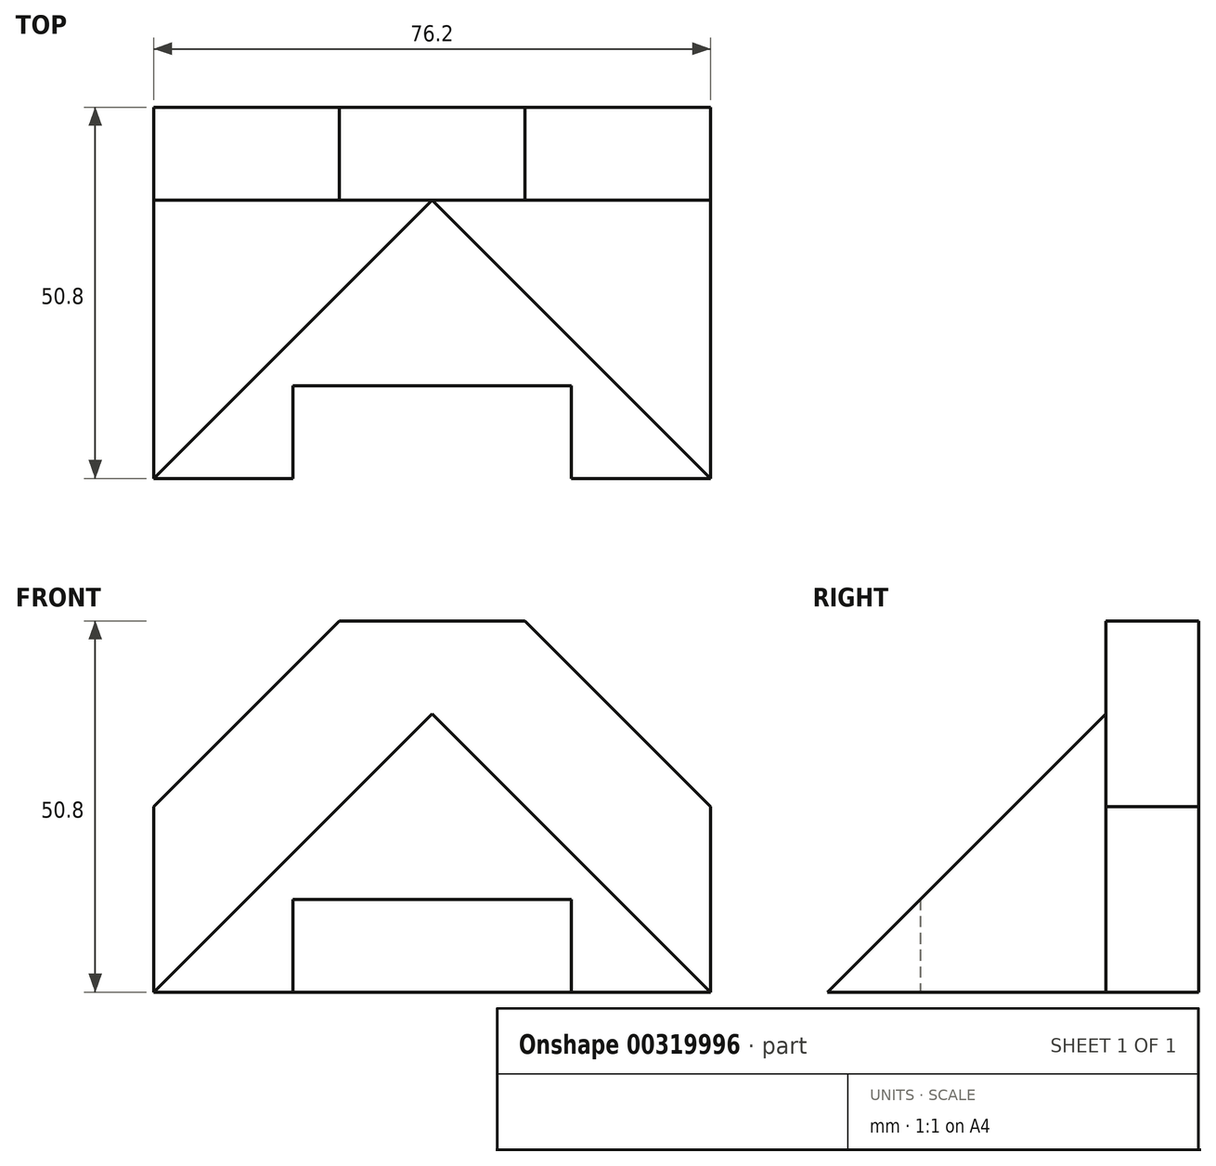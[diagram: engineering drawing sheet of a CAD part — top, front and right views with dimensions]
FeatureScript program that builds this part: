
annotation { "Feature Type Name" : "Feature", "Feature Type Description" : "" }
export const myFeature = defineFeature(function(context is Context, id is Id, definition is map)
    precondition{}
    {
        {
            var Q0;
            Q0=qCreatedBy(makeId("Front.planeOp"),FACE);
            var sketch = newSketch(context, id + "F0", { "sketchPlane" : qUnion([Q0])});
            skLineSegment(sketch, "E0.bottom", {"start": v(0, 0) * mm, "end": v(76.2, 0) * mm});
            skLineSegment(sketch, "E0.top", {"start": v(0, 50.8) * mm, "end": v(76.2, 50.8) * mm});
            skLineSegment(sketch, "E0.left", {"start": v(0, 0) * mm, "end": v(0, 50.8) * mm});
            skLineSegment(sketch, "E0.right", {"start": v(76.2, 0) * mm, "end": v(76.2, 50.8) * mm});
            skSolve(sketch);
        }
        {
            var Q0;
            Q0 = qSketchRegion(id + "F0", true);
            extrude(context, id + "F1", {"entities" : qUnion([Q0]), "depth" : 12.7 * mm});
        }
        {
            var Q0;
            Q0=makeQuery(id+"F1.opExtrude","CAP_FACE",FACE,{"disambiguationData":[OSD([sQuery(id+"F0.wireOp",EDGE,"E0.bottom"),sQuery(id+"F0.wireOp",EDGE,"E0.top"),sQuery(id+"F0.wireOp",EDGE,"E0.left"),sQuery(id+"F0.wireOp",EDGE,"E0.right")])],"isStart":false});
            var sketch = newSketch(context, id + "F2", { "sketchPlane" : qUnion([Q0])});
            skLineSegment(sketch, "E1", {"start": v(0, 25.4) * mm, "end": v(25.4, 50.8) * mm});
            skLineSegment(sketch, "E2", {"start": v(50.8, 50.8) * mm, "end": v(76.2, 25.4) * mm});
            skLineSegment(sketch, "E3", {"start": v(0, 25.4) * mm, "end": v(0, 50.8) * mm});
            skLineSegment(sketch, "E4", {"start": v(0, 50.8) * mm, "end": v(25.4, 50.8) * mm});
            skLineSegment(sketch, "E5", {"start": v(50.8, 50.8) * mm, "end": v(76.2, 50.8) * mm});
            skLineSegment(sketch, "E6", {"start": v(76.2, 50.8) * mm, "end": v(76.2, 25.4) * mm});
            skSolve(sketch);
        }
        {
            var Q0;
            Q0 = qSketchRegion(id + "F2", true);
            extrude(context, id + "F3", {"entities" : qUnion([Q0]), "operationType" : NewBodyOperationType.REMOVE, "oppositeDirection" : true, "depth" : 12.7 * mm});
        }
        {
            var Q0;
            Q0=makeQuery(id+"F1.opExtrude","CAP_FACE",FACE,{"disambiguationData":[OSD([sQuery(id+"F0.wireOp",EDGE,"E0.bottom"),sQuery(id+"F0.wireOp",EDGE,"E0.top"),sQuery(id+"F0.wireOp",EDGE,"E0.left"),sQuery(id+"F0.wireOp",EDGE,"E0.right")])],"isStart":false});
            var sketch = newSketch(context, id + "F4", { "sketchPlane" : qUnion([Q0])});
            skLineSegment(sketch, "E7", {"start": v(0, 0) * mm, "end": v(38.1, 38.1) * mm});
            skLineSegment(sketch, "E8", {"start": v(38.1, 38.1) * mm, "end": v(76.2, 0) * mm});
            skLineSegment(sketch, "E9", {"start": v(0, 0) * mm, "end": v(76.2, 0) * mm});
            skSolve(sketch);
        }
        {
            var Q0;
            Q0 = qSketchRegion(id + "F4", true);
            extrude(context, id + "F5", {"entities" : qUnion([Q0]), "operationType" : NewBodyOperationType.ADD, "depth" : 38.1 * mm});
        }
        {
            var Q0;
            Q0=qCreatedBy(makeId("Right.planeOp"),FACE);
            var sketch = newSketch(context, id + "F6", { "sketchPlane" : qUnion([Q0])});
            skLineSegment(sketch, "E10", {"start": v(-50.8, 0) * mm, "end": v(-12.7, 38.1) * mm});
            skLineSegment(sketch, "E11", {"start": v(-50.8, 0) * mm, "end": v(-50.8, 38.1) * mm});
            skLineSegment(sketch, "E12", {"start": v(-50.8, 38.1) * mm, "end": v(-12.7, 38.1) * mm});
            skSolve(sketch);
        }
        {
            var Q0;
            Q0 = qSketchRegion(id + "F6", true);
            extrude(context, id + "F7", {"entities" : qUnion([Q0]), "operationType" : NewBodyOperationType.REMOVE, "depth" : 76.2 * mm});
        }
        {
            var Q0;
            Q0=qCreatedBy(makeId("Top.planeOp"),FACE);
            var sketch = newSketch(context, id + "F8", { "sketchPlane" : qUnion([Q0])});
            skLineSegment(sketch, "E13.bottom", {"start": v(19.05, -50.8) * mm, "end": v(57.15, -50.8) * mm});
            skLineSegment(sketch, "E13.top", {"start": v(19.05, -38.1) * mm, "end": v(57.15, -38.1) * mm});
            skLineSegment(sketch, "E13.left", {"start": v(19.05, -50.8) * mm, "end": v(19.05, -38.1) * mm});
            skLineSegment(sketch, "E13.right", {"start": v(57.15, -50.8) * mm, "end": v(57.15, -38.1) * mm});
            skSolve(sketch);
        }
        {
            var Q0;
            Q0 = qSketchRegion(id + "F8", true);
            extrude(context, id + "F9", {"entities" : qUnion([Q0]), "operationType" : NewBodyOperationType.REMOVE, "depth" : 12.7 * mm});
        }
    });
